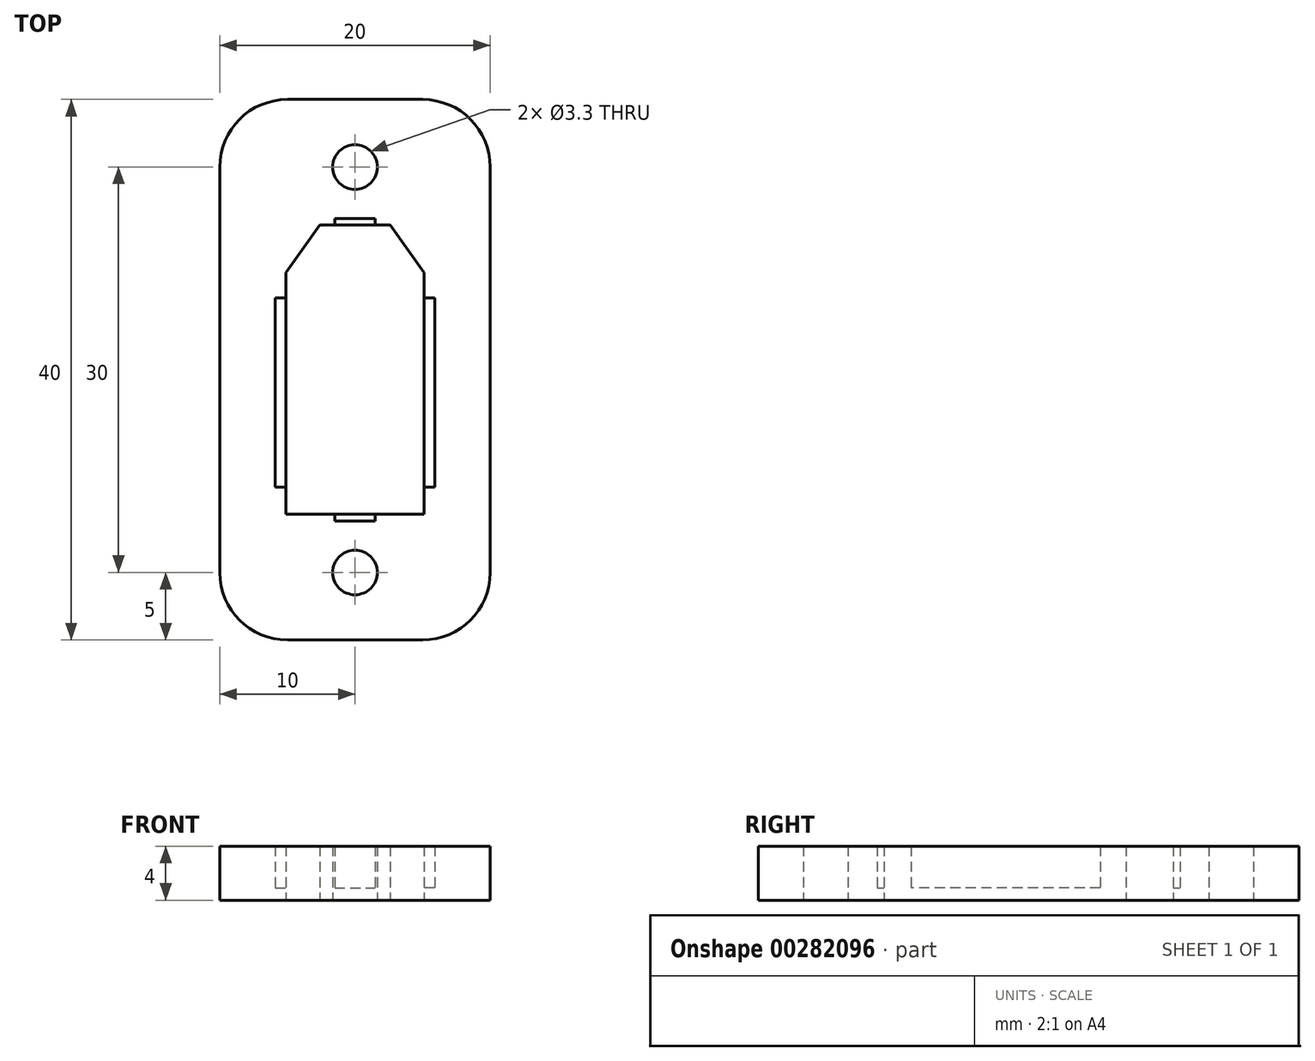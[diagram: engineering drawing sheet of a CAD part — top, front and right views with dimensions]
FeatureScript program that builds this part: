
annotation { "Feature Type Name" : "Feature", "Feature Type Description" : "" }
export const myFeature = defineFeature(function(context is Context, id is Id, definition is map)
    precondition{}
    {
        {
            var Q0;
            Q0=qCreatedBy(makeId("Top.planeOp"),FACE);
            var sketch = newSketch(context, id + "F0", { "sketchPlane" : qUnion([Q0])});
            skLineSegment(sketch, "E0.bottom", {"start": v(-5.1, 10.7) * mm, "end": v(-2.6, 10.7) * mm, "construction": true});
            skLineSegment(sketch, "E0.top", {"start": v(-5.1, -10.7) * mm, "end": v(5.1, -10.7) * mm});
            skLineSegment(sketch, "E0.left", {"start": v(-5.1, 10.7) * mm, "end": v(-5.1, 7.2) * mm, "construction": true});
            skLineSegment(sketch, "E0.right", {"start": v(5.1, 10.7) * mm, "end": v(5.1, 7.2) * mm, "construction": true});
            skPoint(sketch, "E0.middle", {"position": v(0, 0) * mm});
            skLineSegment(sketch, "E1", {"start": v(-5.1, 7.2) * mm, "end": v(-5.1, -10.7) * mm});
            skLineSegment(sketch, "E2", {"start": v(-2.6, 10.7) * mm, "end": v(2.6, 10.7) * mm});
            skLineSegment(sketch, "E3", {"start": v(2.6, 10.7) * mm, "end": v(5.1, 10.7) * mm, "construction": true});
            skLineSegment(sketch, "E4", {"start": v(5.1, 7.2) * mm, "end": v(5.1, -10.7) * mm});
            skLineSegment(sketch, "E5", {"start": v(-5.1, 7.2) * mm, "end": v(-2.6, 10.7) * mm});
            skLineSegment(sketch, "E6", {"start": v(2.6, 10.7) * mm, "end": v(5.1, 7.2) * mm});
            skLineSegment(sketch, "E7.bottom", {"start": v(-10, 20) * mm, "end": v(10, 20) * mm});
            skLineSegment(sketch, "E7.top", {"start": v(-10, -20) * mm, "end": v(10, -20) * mm});
            skLineSegment(sketch, "E7.left", {"start": v(-10, 20) * mm, "end": v(-10, -20) * mm});
            skLineSegment(sketch, "E7.right", {"start": v(10, 20) * mm, "end": v(10, -20) * mm});
            skCircle(sketch, "E8", {"center": v(0, 15) * mm, "radius": 1.65 * mm});
            skCircle(sketch, "E9", {"center": v(0, -15) * mm, "radius": 1.65 * mm});
            skSolve(sketch);
        }
        {
            var Q0;
            Q0 = qSketchRegion(id + "F0", true);
            extrude(context, id + "F1", {"entities" : qUnion([Q0]), "depth" : 4 * mm, "offsetDistance" : 25 * mm});
        }
        {
            var Q0;
            Q0=makeQuery(id+"F1.opExtrude","SWEPT_EDGE",EDGE,{"disambiguationData":[OSD([sQuery(id+"F0.wireOp",EDGE,"E7.bottom"),sQuery(id+"F0.wireOp",EDGE,"E7.left")])]});
            var Q1;
            Q1=makeQuery(id+"F1.opExtrude","SWEPT_EDGE",EDGE,{"disambiguationData":[OSD([sQuery(id+"F0.wireOp",EDGE,"E7.top"),sQuery(id+"F0.wireOp",EDGE,"E7.left")])]});
            var Q2;
            Q2=makeQuery(id+"F1.opExtrude","SWEPT_EDGE",EDGE,{"disambiguationData":[OSD([sQuery(id+"F0.wireOp",EDGE,"E7.top"),sQuery(id+"F0.wireOp",EDGE,"E7.right")])]});
            var Q3;
            Q3=makeQuery(id+"F1.opExtrude","SWEPT_EDGE",EDGE,{"disambiguationData":[OSD([sQuery(id+"F0.wireOp",EDGE,"E7.bottom"),sQuery(id+"F0.wireOp",EDGE,"E7.right")])]});
            fillet(context, id + "F2", {"entities" : qUnion([Q0, Q1, Q2, Q3]), "radius" : 5 * mm, "tangentPropagation" : true, "allowEdgeOverflow" : false});
        }
        {
            var Q0;
            Q0=qCreatedBy(makeId("Top.planeOp"),FACE);
            cPlane(context, id + "F3", {"entities" : qUnion([Q0]), "cplaneType" : CPlaneType.OFFSET, "offset" : 0.9 * mm, "width" : 150 * mm, "height" : 150 * mm});
        }
        {
            var Q0;
            Q0=qCreatedBy(id+"F3.planeOp",FACE);
            var sketch = newSketch(context, id + "F4", { "sketchPlane" : qUnion([Q0])});
            skLineSegment(sketch, "E10.bottom", {"start": v(-5.1, 10.7) * mm, "end": v(-2.6, 10.7) * mm, "construction": true});
            skLineSegment(sketch, "E10.top", {"start": v(-5.1, -10.7) * mm, "end": v(5.1, -10.7) * mm});
            skLineSegment(sketch, "E10.left", {"start": v(-5.1, 10.7) * mm, "end": v(-5.1, 7.2) * mm, "construction": true});
            skLineSegment(sketch, "E10.right", {"start": v(5.1, 10.7) * mm, "end": v(5.1, 7.2) * mm, "construction": true});
            skPoint(sketch, "E10.middle", {"position": v(0, 0) * mm});
            skLineSegment(sketch, "E11", {"start": v(-5.1, 7.2) * mm, "end": v(-5.1, -10.7) * mm});
            skLineSegment(sketch, "E12", {"start": v(-2.6, 10.7) * mm, "end": v(2.6, 10.7) * mm});
            skLineSegment(sketch, "E13", {"start": v(2.6, 10.7) * mm, "end": v(5.1, 10.7) * mm, "construction": true});
            skLineSegment(sketch, "E14", {"start": v(5.1, 7.2) * mm, "end": v(5.1, -10.7) * mm});
            skLineSegment(sketch, "E15", {"start": v(-5.1, 7.2) * mm, "end": v(-2.6, 10.7) * mm});
            skLineSegment(sketch, "E16", {"start": v(2.6, 10.7) * mm, "end": v(5.1, 7.2) * mm});
            skLineSegment(sketch, "E17.bottom", {"start": v(-10, 15.5) * mm, "end": v(10, 15.5) * mm});
            skLineSegment(sketch, "E17.top", {"start": v(-10, -15.5) * mm, "end": v(10, -15.5) * mm});
            skLineSegment(sketch, "E17.left", {"start": v(-10, 15.5) * mm, "end": v(-10, -15.5) * mm});
            skLineSegment(sketch, "E17.right", {"start": v(10, 15.5) * mm, "end": v(10, -15.5) * mm});
            skLineSegment(sketch, "E18", {"start": v(-5.1, -8.7) * mm, "end": v(-5.9, -8.7) * mm});
            skLineSegment(sketch, "E19", {"start": v(-5.9, -8.7) * mm, "end": v(-5.9, 5.3) * mm});
            skLineSegment(sketch, "E20", {"start": v(-5.9, 5.3) * mm, "end": v(-5.1, 5.3) * mm});
            skLineSegment(sketch, "E21", {"start": v(-5.1, 5.3) * mm, "end": v(5.1, 5.3) * mm, "construction": true});
            skLineSegment(sketch, "E22", {"start": v(-5.1, -8.7) * mm, "end": v(5.1, -8.7) * mm, "construction": true});
            skLineSegment(sketch, "E23", {"start": v(5.1, -8.7) * mm, "end": v(5.9, -8.7) * mm});
            skLineSegment(sketch, "E24", {"start": v(5.9, -8.7) * mm, "end": v(5.9, 5.3) * mm});
            skLineSegment(sketch, "E25", {"start": v(5.9, 5.3) * mm, "end": v(5.1, 5.3) * mm});
            skLineSegment(sketch, "E26", {"start": v(-1.5, 10.7) * mm, "end": v(-1.5, 11.2) * mm});
            skLineSegment(sketch, "E27", {"start": v(-1.5, 11.2) * mm, "end": v(1.5, 11.2) * mm});
            skLineSegment(sketch, "E28", {"start": v(1.5, 11.2) * mm, "end": v(1.5, 10.7) * mm});
            skLineSegment(sketch, "E29", {"start": v(-1.5, -10.7) * mm, "end": v(-1.5, -11.2) * mm});
            skLineSegment(sketch, "E30", {"start": v(-1.5, -11.2) * mm, "end": v(1.5, -11.2) * mm});
            skLineSegment(sketch, "E31", {"start": v(1.5, -11.2) * mm, "end": v(1.5, -10.7) * mm});
            skSolve(sketch);
        }
        {
            var Q0;
            {var subQ6=sQuery(id+"F4.wireOp",EDGE,"E15");Q0=makeQuery(id+"F4.imprint","IMPRINT",FACE,{"disambiguationData":[TD([[makeQuery(id+"F4.imprint","IMPRINT",EDGE,{"derivedFrom":subQ6}),-1.0]])]});}
            var Q1;
            {var subQ0=sQuery(id+"F4.wireOp",EDGE,"E18");Q1=makeQuery(id+"F4.imprint","IMPRINT",FACE,{"disambiguationData":[TD([[makeQuery(id+"F4.imprint","IMPRINT",EDGE,{"derivedFrom":subQ0}),-1.0]])]});}
            var Q2;
            {var subQ0=sQuery(id+"F4.wireOp",EDGE,"E26");Q2=makeQuery(id+"F4.imprint","IMPRINT",FACE,{"disambiguationData":[TD([[makeQuery(id+"F4.imprint","IMPRINT",EDGE,{"derivedFrom":subQ0}),-1.0]])]});}
            var Q3;
            {var subQ0=sQuery(id+"F4.wireOp",EDGE,"E23");Q3=makeQuery(id+"F4.imprint","IMPRINT",FACE,{"disambiguationData":[TD([[makeQuery(id+"F4.imprint","IMPRINT",EDGE,{"derivedFrom":subQ0}),1.0]])]});}
            var Q4;
            {var subQ0=sQuery(id+"F4.wireOp",EDGE,"E29");Q4=makeQuery(id+"F4.imprint","IMPRINT",FACE,{"disambiguationData":[TD([[makeQuery(id+"F4.imprint","IMPRINT",EDGE,{"derivedFrom":subQ0}),1.0]])]});}
            extrude(context, id + "F5", {"entities" : qUnion([Q0, Q1, Q2, Q3, Q4]), "operationType" : NewBodyOperationType.REMOVE, "depth" : 3.5 * mm, "offsetDistance" : 25 * mm});
        }
    });
